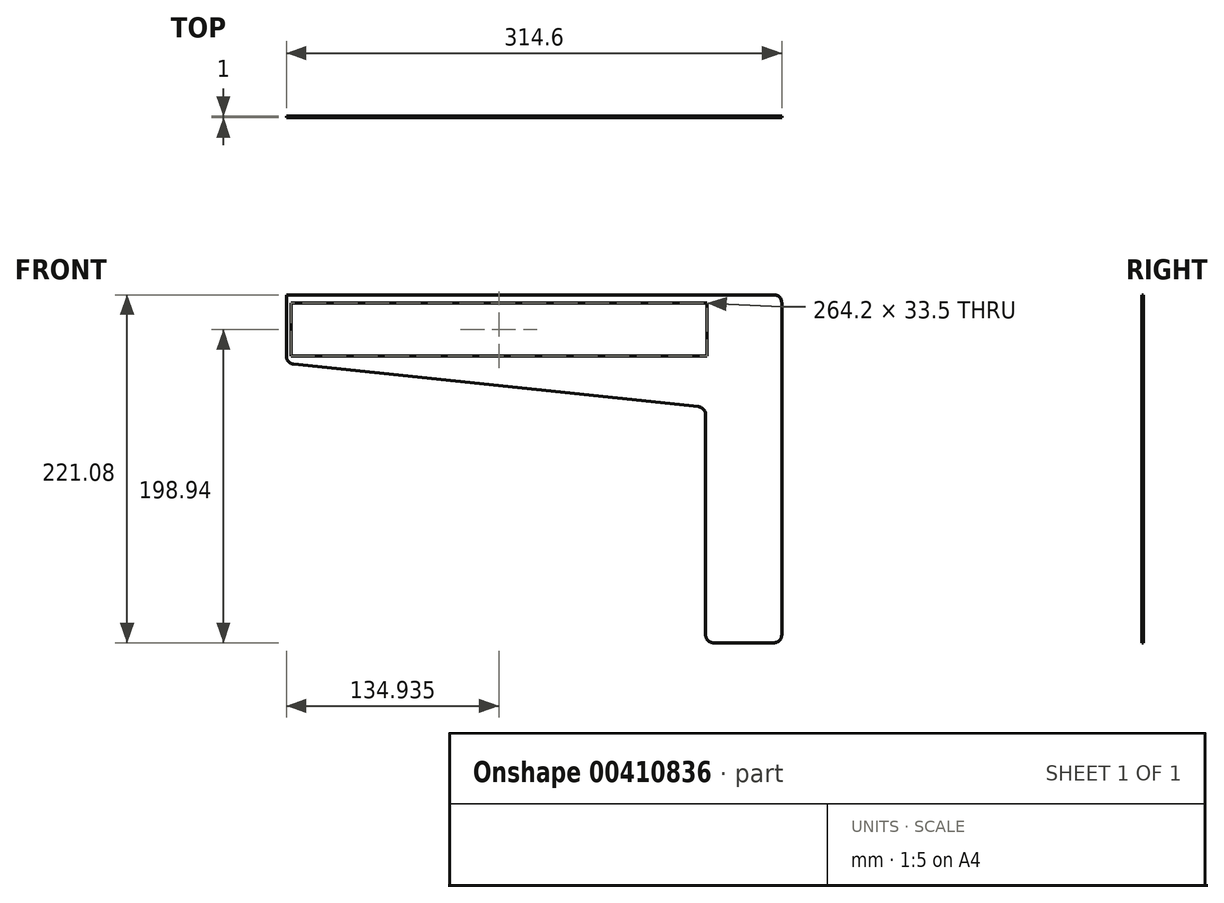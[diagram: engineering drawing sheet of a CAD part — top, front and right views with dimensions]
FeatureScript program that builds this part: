
annotation { "Feature Type Name" : "Feature", "Feature Type Description" : "" }
export const myFeature = defineFeature(function(context is Context, id is Id, definition is map)
    precondition{}
    {
        {
            var Q0;
            Q0=qCreatedBy(makeId("Front.planeOp"),FACE);
            var sketch = newSketch(context, id + "F0", { "sketchPlane" : qUnion([Q0])});
            skLineSegment(sketch, "E0", {"start": v(0, 0) * mm, "end": v(309.6, 0) * mm});
            skLineSegment(sketch, "E1", {"start": v(0, 0) * mm, "end": v(0, -39.1) * mm});
            skLineSegment(sketch, "E2", {"start": v(4.48, -44.07) * mm, "end": v(261.8, -71.1) * mm});
            skLineSegment(sketch, "E3", {"start": v(266.28, -76.08) * mm, "end": v(266.28, -216.08) * mm});
            skLineSegment(sketch, "E4", {"start": v(271.28, -221.08) * mm, "end": v(309.6, -221.08) * mm});
            skLineSegment(sketch, "E5", {"start": v(314.6, -216.08) * mm, "end": v(314.6, -5) * mm});
            skPoint(sketch, "E6.visualSharp", {"position": v(266.28, -71.58) * mm});
            skArc(sketch, "E6.filletArc", {"start": v(266.28, -76.08) * mm, "mid": v(265, -72.73) * mm, "end": v(261.8, -71.1) * mm});
            skPoint(sketch, "E7.visualSharp", {"position": v(0, -43.6) * mm});
            skArc(sketch, "E7.filletArc", {"start": v(0, -39.1) * mm, "mid": v(1.28, -42.44) * mm, "end": v(4.48, -44.07) * mm});
            skPoint(sketch, "E8.visualSharp", {"position": v(314.6, 0) * mm});
            skArc(sketch, "E8.filletArc", {"start": v(314.6, -5) * mm, "mid": v(313.14, -1.46) * mm, "end": v(309.6, 0) * mm});
            skPoint(sketch, "E9.visualSharp", {"position": v(314.6, -221.08) * mm});
            skArc(sketch, "E9.filletArc", {"start": v(309.6, -221.08) * mm, "mid": v(313.14, -219.62) * mm, "end": v(314.6, -216.08) * mm});
            skPoint(sketch, "E10.visualSharp", {"position": v(266.28, -221.08) * mm});
            skArc(sketch, "E10.filletArc", {"start": v(266.28, -216.08) * mm, "mid": v(267.75, -219.62) * mm, "end": v(271.28, -221.08) * mm});
            skLineSegment(sketch, "E11.bottom", {"start": v(267.04, -38.9) * mm, "end": v(2.84, -38.9) * mm});
            skLineSegment(sketch, "E11.top", {"start": v(267.04, -5.4) * mm, "end": v(2.84, -5.4) * mm});
            skLineSegment(sketch, "E11.left", {"start": v(267.04, -38.9) * mm, "end": v(267.04, -5.4) * mm});
            skLineSegment(sketch, "E11.right", {"start": v(2.84, -38.9) * mm, "end": v(2.84, -5.4) * mm});
            skSolve(sketch);
        }
        {
            var Q0;
            Q0=makeQuery(id+"F0.imprint","IMPRINT",FACE,{"disambiguationData":[TD([[makeQuery(id+"F0.imprint","IMPRINT",EDGE,{"derivedFrom":sQuery(id+"F0.wireOp",EDGE,"E0")}),-1.0]])]});
            extrude(context, id + "F1", {"entities" : qUnion([Q0]), "depth" : 1 * mm});
        }
    });
